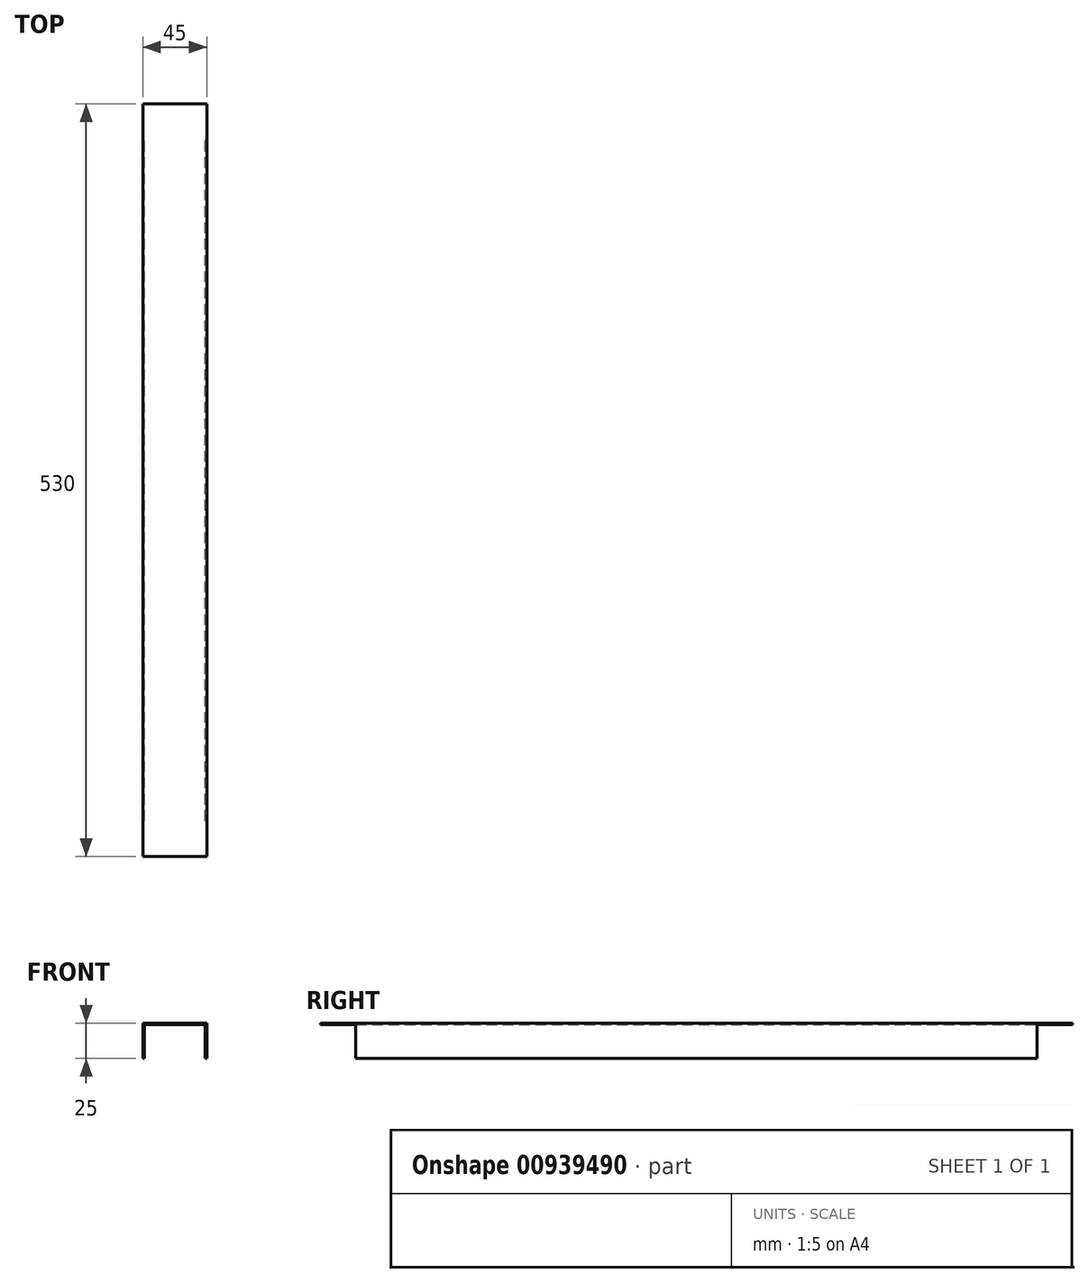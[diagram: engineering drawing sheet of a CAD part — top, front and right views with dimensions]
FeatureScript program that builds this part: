
annotation { "Feature Type Name" : "Feature", "Feature Type Description" : "" }
export const myFeature = defineFeature(function(context is Context, id is Id, definition is map)
    precondition{}
    {
        {
            var Q0;
            Q0=qCreatedBy(makeId("Top.planeOp"),FACE);
            var sketch = newSketch(context, id + "F0", { "sketchPlane" : qUnion([Q0])});
            skLineSegment(sketch, "E0.bottom", {"start": v(0, 0) * mm, "end": v(45, 0) * mm});
            skLineSegment(sketch, "E0.top", {"start": v(0, 530) * mm, "end": v(45, 530) * mm});
            skLineSegment(sketch, "E0.left", {"start": v(0, 0) * mm, "end": v(0, 530) * mm});
            skLineSegment(sketch, "E0.right", {"start": v(45, 0) * mm, "end": v(45, 530) * mm});
            skSolve(sketch);
        }
        {
            var Q0;
            Q0=makeQuery(id+"F0.imprint","IMPRINT",FACE,{"disambiguationData":[TD([[makeQuery(id+"F0.imprint","IMPRINT",EDGE,{"derivedFrom":sQuery(id+"F0.wireOp",EDGE,"E0.bottom")}),1.0]])]});
            extrude(context, id + "F1", {"entities" : qUnion([Q0]), "oppositeDirection" : true, "depth" : 25 * mm, "offsetDistance" : 25 * mm});
        }
        {
            var Q0;
            Q0=makeQuery(id+"F1.opExtrude","SWEPT_FACE",FACE,{"disambiguationData":[OSD([sQuery(id+"F0.wireOp",EDGE,"E0.bottom")])]});
            var sketch = newSketch(context, id + "F2", { "sketchPlane" : qUnion([Q0])});
            skLineSegment(sketch, "E1.bottom", {"start": v(0, 0) * mm, "end": v(45, 0) * mm});
            skLineSegment(sketch, "E1.top", {"start": v(0, -1) * mm, "end": v(45, -1) * mm});
            skLineSegment(sketch, "E1.left", {"start": v(0, 0) * mm, "end": v(0, -1) * mm});
            skLineSegment(sketch, "E1.right", {"start": v(45, 0) * mm, "end": v(45, -1) * mm});
            skSolve(sketch);
        }
        {
            var Q0;
            {var subQ0=sQuery(id+"F2.wireOp",EDGE,"E1.top");Q0=makeQuery(id+"F2.imprint","IMPRINT",FACE,{"disambiguationData":[TD([[makeQuery(id+"F2.imprint","IMPRINT",EDGE,{"derivedFrom":subQ0}),-1.0]])]});}
            extrude(context, id + "F3", {"entities" : qUnion([Q0]), "operationType" : NewBodyOperationType.REMOVE, "oppositeDirection" : true, "depth" : 25 * mm, "offsetDistance" : 25 * mm});
        }
        {
            var Q0;
            Q0=makeQuery(id+"F1.opExtrude","SWEPT_FACE",FACE,{"disambiguationData":[OSD([sQuery(id+"F0.wireOp",EDGE,"E0.top")])]});
            var sketch = newSketch(context, id + "F4", { "sketchPlane" : qUnion([Q0])});
            skLineSegment(sketch, "E2.bottom", {"start": v(-45, 0) * mm, "end": v(0, 0) * mm});
            skLineSegment(sketch, "E2.top", {"start": v(-45, -1) * mm, "end": v(0, -1) * mm});
            skLineSegment(sketch, "E2.left", {"start": v(-45, 0) * mm, "end": v(-45, -1) * mm});
            skLineSegment(sketch, "E2.right", {"start": v(0, 0) * mm, "end": v(0, -1) * mm});
            skSolve(sketch);
        }
        {
            var Q0;
            {var subQ0=sQuery(id+"F4.wireOp",EDGE,"E2.top");Q0=makeQuery(id+"F4.imprint","IMPRINT",FACE,{"disambiguationData":[TD([[makeQuery(id+"F4.imprint","IMPRINT",EDGE,{"derivedFrom":subQ0}),-1.0]])]});}
            extrude(context, id + "F5", {"entities" : qUnion([Q0]), "operationType" : NewBodyOperationType.REMOVE, "oppositeDirection" : true, "depth" : 25 * mm, "offsetDistance" : 25 * mm});
        }
        {
            var Q0;
            Q0=makeQuery(id+"F5.boolean.opBoolean","COPY",FACE,{"derivedFrom":makeQuery(id+"F5.opExtrude","CAP_FACE",FACE,{"disambiguationData":[OSD([sQuery(id+"F0.wireOp",EDGE,"E0.top"),sQuery(id+"F0.wireOp",EDGE,"E0.left"),sQuery(id+"F0.wireOp",EDGE,"E0.right"),sQuery(id+"F4.wireOp",EDGE,"E2.top")])],"isStart":false})});
            var sketch = newSketch(context, id + "F6", { "sketchPlane" : qUnion([Q0])});
            skLineSegment(sketch, "E3.bottom", {"start": v(-44, -25) * mm, "end": v(-1, -25) * mm});
            skLineSegment(sketch, "E3.top", {"start": v(-44, -1) * mm, "end": v(-1, -1) * mm});
            skLineSegment(sketch, "E3.left", {"start": v(-44, -25) * mm, "end": v(-44, -1) * mm});
            skLineSegment(sketch, "E3.right", {"start": v(-1, -25) * mm, "end": v(-1, -1) * mm});
            skSolve(sketch);
        }
        {
            var Q0;
            Q0=makeQuery(id+"F6.imprint","IMPRINT",FACE,{"disambiguationData":[TD([[makeQuery(id+"F6.imprint","IMPRINT",EDGE,{"derivedFrom":sQuery(id+"F6.wireOp",EDGE,"E3.bottom")}),-1.0]])]});
            extrude(context, id + "F7", {"entities" : qUnion([Q0]), "operationType" : NewBodyOperationType.REMOVE, "endBound" : BoundingType.THROUGH_ALL, "oppositeDirection" : true, "depth" : 25 * mm, "offsetDistance" : 25 * mm});
        }
    });
